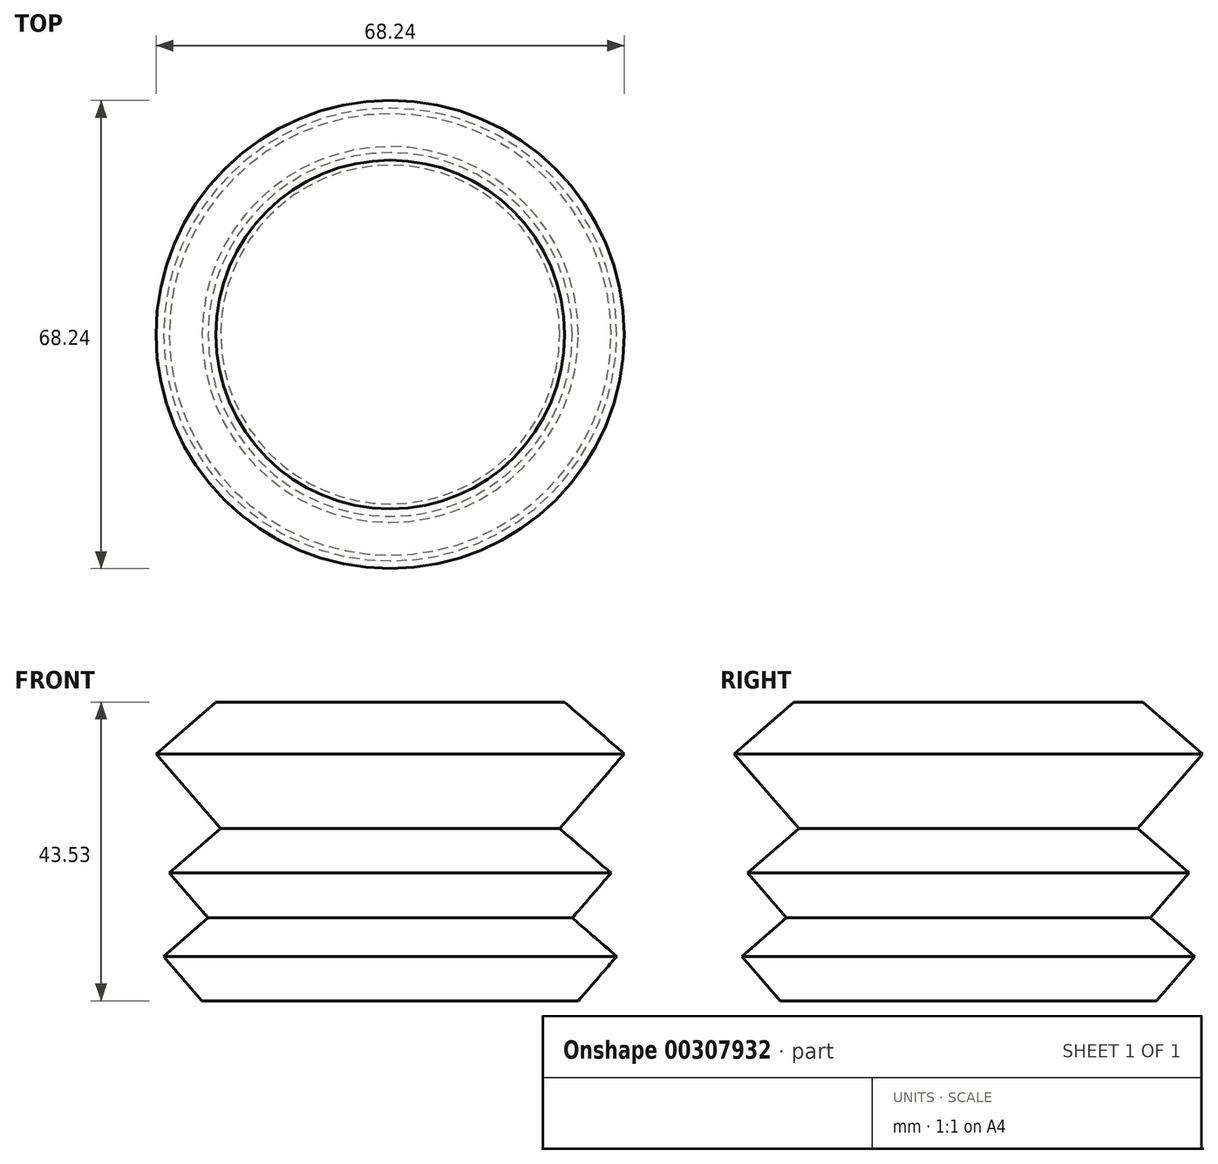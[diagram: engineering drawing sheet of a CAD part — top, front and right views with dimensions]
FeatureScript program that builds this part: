
annotation { "Feature Type Name" : "Feature", "Feature Type Description" : "" }
export const myFeature = defineFeature(function(context is Context, id is Id, definition is map)
    precondition{}
    {
        {
            var Q0;
            Q0=qCreatedBy(makeId("Front.planeOp"),FACE);
            var sketch = newSketch(context, id + "F0", { "sketchPlane" : qUnion([Q0])});
            skLineSegment(sketch, "E0", {"start": v(-27.4, 0) * mm, "end": v(0, 0) * mm});
            skLineSegment(sketch, "E1", {"start": v(0, 0) * mm, "end": v(-27.4, 0) * mm});
            skLineSegment(sketch, "E2", {"start": v(-33, 6.48) * mm, "end": v(-27.4, 0) * mm});
            skLineSegment(sketch, "E3", {"start": v(-33, 6.48) * mm, "end": v(-26.53, 12.07) * mm});
            skLineSegment(sketch, "E4", {"start": v(-26.53, 12.07) * mm, "end": v(-32.19, 18.63) * mm});
            skLineSegment(sketch, "E5", {"start": v(-32.19, 18.63) * mm, "end": v(-24.7, 25.1) * mm});
            skLineSegment(sketch, "E6", {"start": v(-24.7, 25.1) * mm, "end": v(-34.12, 36) * mm});
            skLineSegment(sketch, "E7", {"start": v(-34.12, 36) * mm, "end": v(-25.42, 43.53) * mm});
            skLineSegment(sketch, "E8", {"start": v(-25.42, 43.53) * mm, "end": v(0, 43.53) * mm});
            skLineSegment(sketch, "E9", {"start": v(0, 43.53) * mm, "end": v(0, 0) * mm});
            skSolve(sketch);
        }
        {
            var Q0;
            Q0 = qSketchRegion(id + "F0", true);
            var Q1;
            Q1=sQuery(id+"F0.wireOp",EDGE,"E9");
            revolve(context, id + "F1", {"entities" : qUnion([Q0]), "axis" : qUnion([Q1]), "revolveType" : RevolveType.FULL});
        }
    });
